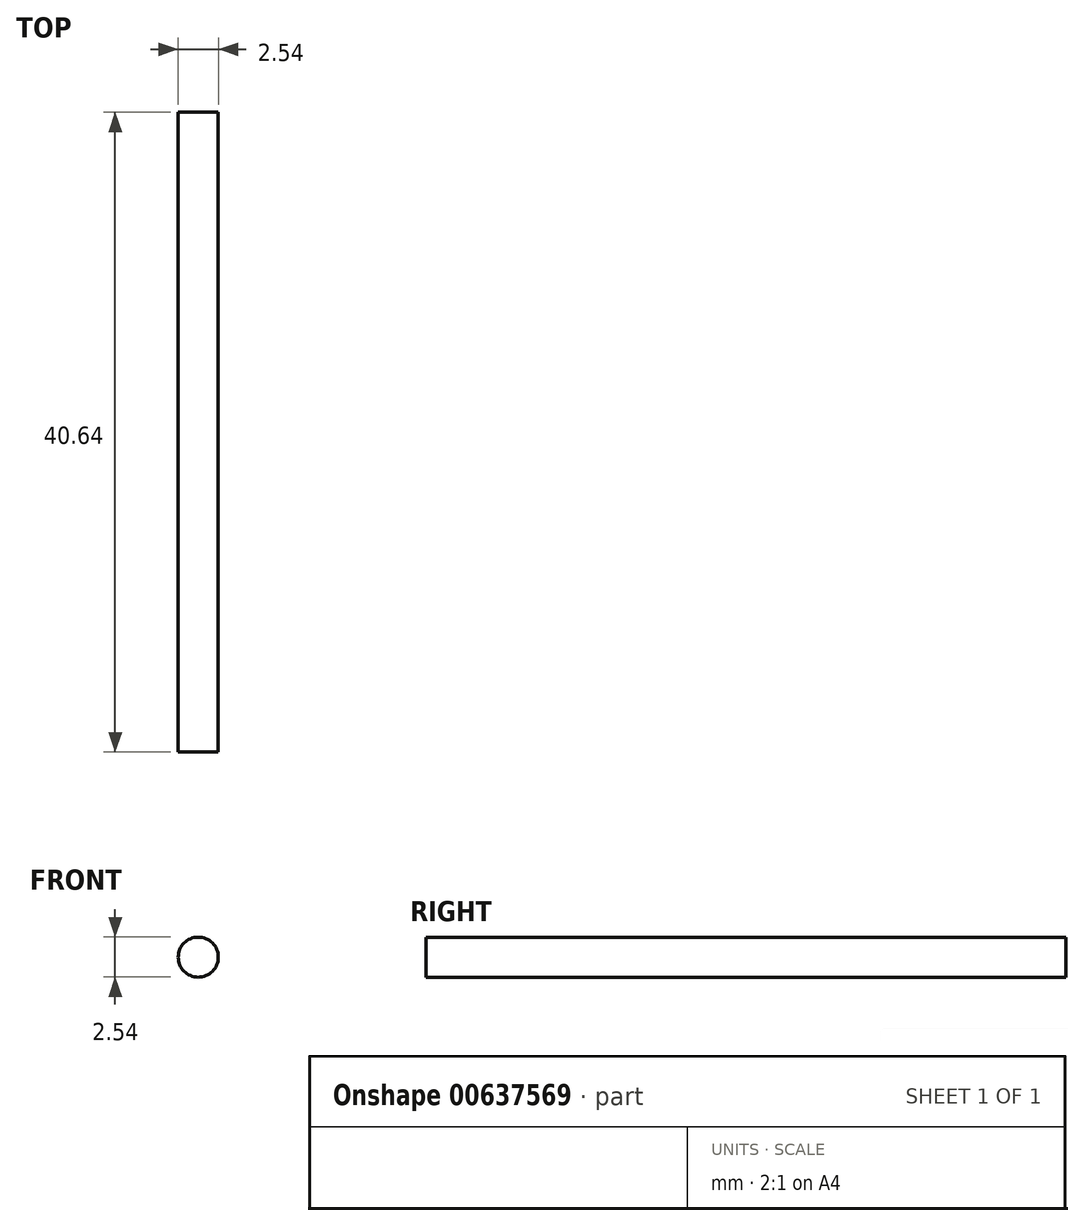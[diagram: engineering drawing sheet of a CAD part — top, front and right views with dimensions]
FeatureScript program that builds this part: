
annotation { "Feature Type Name" : "Feature", "Feature Type Description" : "" }
export const myFeature = defineFeature(function(context is Context, id is Id, definition is map)
    precondition{}
    {
        {
            var Q0;
            Q0=qCreatedBy(makeId("Front.planeOp"),FACE);
            var sketch = newSketch(context, id + "F0", { "sketchPlane" : qUnion([Q0])});
            skCircle(sketch, "E0", {"center": v(-36, 6.02) * mm, "radius": 1.27 * mm});
            skSolve(sketch);
        }
        {
            var Q0;
            Q0 = qSketchRegion(id + "F0", true);
            extrude(context, id + "F1", {"entities" : qUnion([Q0]), "depth" : 40.64 * mm, "offsetDistance" : 25.4 * mm});
        }
    });
